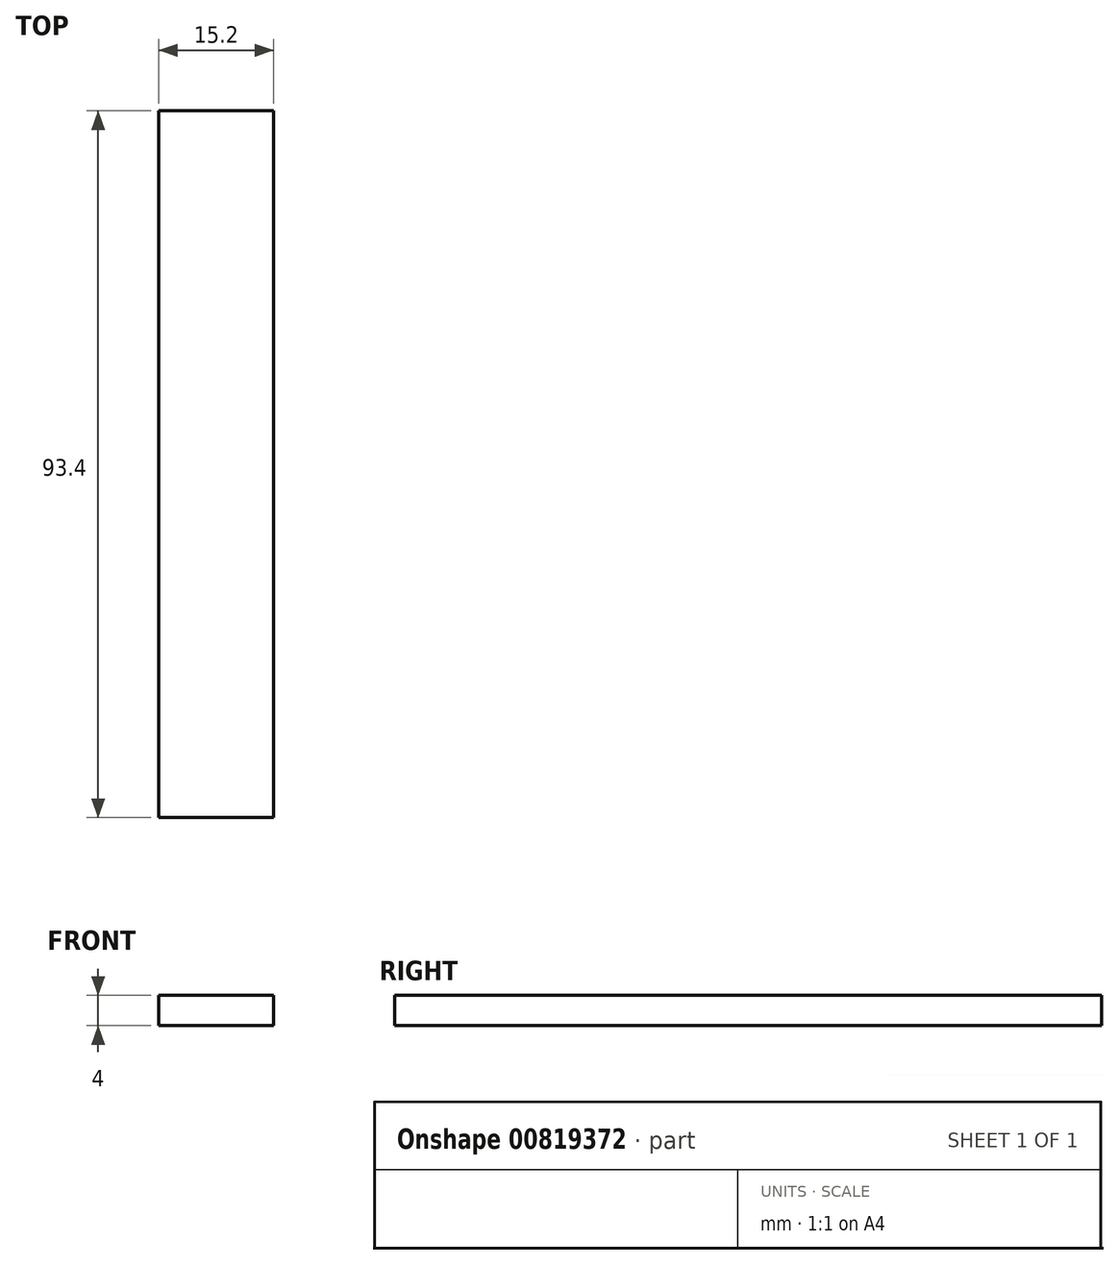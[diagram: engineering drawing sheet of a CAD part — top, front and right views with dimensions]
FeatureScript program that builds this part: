
annotation { "Feature Type Name" : "Feature", "Feature Type Description" : "" }
export const myFeature = defineFeature(function(context is Context, id is Id, definition is map)
    precondition{}
    {
        {
            var Q0;
            Q0=qCreatedBy(makeId("Top.planeOp"),FACE);
            var sketch = newSketch(context, id + "F0", { "sketchPlane" : qUnion([Q0])});
            skLineSegment(sketch, "E0.bottom", {"start": v(-1.26, 85.1) * mm, "end": v(13.94, 85.1) * mm});
            skLineSegment(sketch, "E0.top", {"start": v(-1.26, -8.3) * mm, "end": v(13.94, -8.3) * mm});
            skLineSegment(sketch, "E0.left", {"start": v(-1.26, 85.1) * mm, "end": v(-1.26, -8.3) * mm});
            skLineSegment(sketch, "E0.right", {"start": v(13.94, 85.1) * mm, "end": v(13.94, -8.3) * mm});
            skSolve(sketch);
        }
        {
            var Q0;
            Q0=makeQuery(id+"F0.imprint","IMPRINT",FACE,{"disambiguationData":[TD([[makeQuery(id+"F0.imprint","IMPRINT",EDGE,{"derivedFrom":sQuery(id+"F0.wireOp",EDGE,"E0.bottom")}),-1.0]])]});
            extrude(context, id + "F1", {"entities" : qUnion([Q0]), "depth" : 4 * mm, "offsetDistance" : 25.4 * mm});
        }
    });
